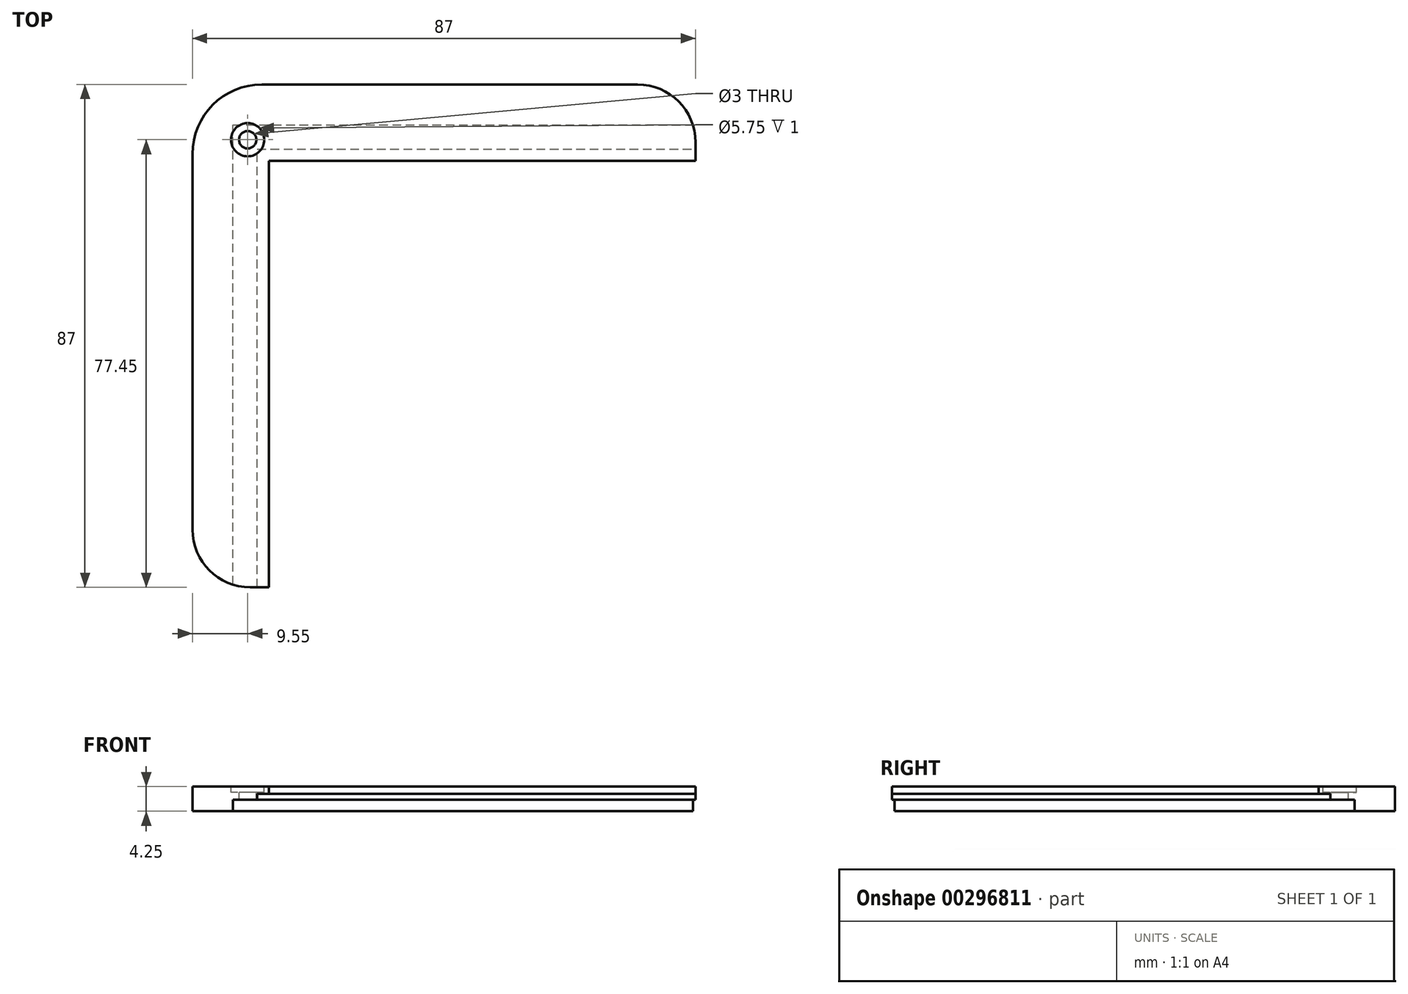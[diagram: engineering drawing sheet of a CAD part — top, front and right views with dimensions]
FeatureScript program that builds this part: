
annotation { "Feature Type Name" : "Feature", "Feature Type Description" : "" }
export const myFeature = defineFeature(function(context is Context, id is Id, definition is map)
    precondition{}
    {
        {
            var Q0;
            Q0=qCreatedBy(makeId("Front.planeOp"),FACE);
            var sketch = newSketch(context, id + "F0", { "sketchPlane" : qUnion([Q0])});
            skLineSegment(sketch, "E0", {"start": v(-6.2, -1) * mm, "end": v(-6.2, -3) * mm});
            skLineSegment(sketch, "E1", {"start": v(-6.2, -3) * mm, "end": v(-13.2, -3) * mm});
            skLineSegment(sketch, "E2", {"start": v(-13.2, -3) * mm, "end": v(-13.2, 1.25) * mm});
            skLineSegment(sketch, "E3", {"start": v(-13.2, 1.25) * mm, "end": v(0, 1.25) * mm});
            skLineSegment(sketch, "E4", {"start": v(0, 1.25) * mm, "end": v(0, 0) * mm});
            skLineSegment(sketch, "E5", {"start": v(-6.2, -1) * mm, "end": v(-2, -1) * mm});
            skLineSegment(sketch, "E6", {"start": v(-2, -1) * mm, "end": v(-2, 0) * mm});
            skLineSegment(sketch, "E7", {"start": v(-2, 0) * mm, "end": v(0, 0) * mm});
            skSolve(sketch);
        }
        {
            var Q0;
            Q0=qCreatedBy(makeId("Top.planeOp"),FACE);
            var sketch = newSketch(context, id + "F1", { "sketchPlane" : qUnion([Q0])});
            skPoint(sketch, "E8.0", {"position": v(-6.2, 0) * mm});
            skLineSegment(sketch, "E9", {"start": v(-6.2, 0) * mm, "end": v(-6.2, 80) * mm});
            skLineSegment(sketch, "E10", {"start": v(-6.2, 80) * mm, "end": v(73.8, 80) * mm});
            skSolve(sketch);
        }
        {
            var Q0;
            Q0 = qSketchRegion(id + "F0", true);
            var Q1;
            Q1 = qConstructionFilter(qBodyType(qCreatedBy(id + "F1" ,EDGE), BodyType.WIRE), ConstructionObject.NO);
            sweep(context, id + "F2", {"profiles" : qUnion([Q0]), "path" : qUnion([Q1])});
        }
        {
            var Q0;
            Q0=makeQuery(id+"F2.opSweep","CAP_EDGE",EDGE,{"disambiguationData":[OSD([sQuery(id+"F0.wireOp",EDGE,"E2"),sQuery(id+"F1.wireOp",VERTEX,"E9.start")])],"isStart":true});
            var Q1;
            Q1=makeQuery(id+"F2.opSweep","CAP_EDGE",EDGE,{"disambiguationData":[OSD([sQuery(id+"F0.wireOp",EDGE,"E2"),sQuery(id+"F1.wireOp",VERTEX,"E10.end")])],"isStart":false});
            fillet(context, id + "F3", {"entities" : qUnion([Q0, Q1]), "radius" : 10 * mm, "tangentPropagation" : true, "allowEdgeOverflow" : false});
        }
        {
            var Q0;
            Q0=makeQuery(id+"F2.opSweep","MID_CAP_EDGE",EDGE,{"disambiguationData":[OSD([sQuery(id+"F0.wireOp",EDGE,"E2"),sQuery(id+"F1.wireOp",VERTEX,"E10.start")])],"capPos":1.0});
            fillet(context, id + "F4", {"entities" : qUnion([Q0]), "radius" : 12 * mm, "tangentPropagation" : true, "allowEdgeOverflow" : false});
        }
        {
            var Q0;
            Q0=makeQuery(id+"F2.opSweep","SWEPT_FACE",FACE,{"disambiguationData":[OSD([sQuery(id+"F0.wireOp",EDGE,"E3"),sQuery(id+"F1.wireOp",EDGE,"E9")])]});
            var sketch = newSketch(context, id + "F5", { "sketchPlane" : qUnion([Q0])});
            skPoint(sketch, "E11.0", {"position": v(-6.2, 80) * mm});
            skLineSegment(sketch, "E12.bottom", {"start": v(-6.2, 80) * mm, "end": v(-3.65, 80) * mm, "construction": true});
            skLineSegment(sketch, "E12.top", {"start": v(-6.2, 77.45) * mm, "end": v(-3.65, 77.45) * mm, "construction": true});
            skLineSegment(sketch, "E12.left", {"start": v(-6.2, 80) * mm, "end": v(-6.2, 77.45) * mm, "construction": true});
            skLineSegment(sketch, "E12.right", {"start": v(-3.65, 80) * mm, "end": v(-3.65, 77.45) * mm, "construction": true});
            skPoint(sketch, "E13", {"position": v(-3.65, 77.45) * mm});
            skSolve(sketch);
        }
        {
            var Q0;
            Q0=sQuery(id+"F5.wireOp",VERTEX,"E13");
            var Q1;
            Q1=makeQuery(id+"F2.opSweep","SWEPT_BODY",BODY,{"disambiguationData":[OSD([sQuery(id+"F0.wireOp",EDGE,"E0"),sQuery(id+"F0.wireOp",EDGE,"E1"),sQuery(id+"F0.wireOp",EDGE,"E2"),sQuery(id+"F0.wireOp",EDGE,"E3"),sQuery(id+"F0.wireOp",EDGE,"E4"),sQuery(id+"F0.wireOp",EDGE,"E5"),sQuery(id+"F0.wireOp",EDGE,"E6"),sQuery(id+"F0.wireOp",EDGE,"E7"),sQuery(id+"F1.wireOp",EDGE,"E10")])]});
            hole(context, id + "F6", {"style" : HoleStyle.C_BORE, "endStyle" : HoleEndStyle.THROUGH, "holeDiameter" : 3 * mm, "cBoreDiameter" : 5.75 * mm, "cBoreDepth" : 1 * mm, "tappedDepth" : 12 * mm, "tapClearance" : 3, "startFromSketch" : true, "locations" : qUnion([Q0]), "scope" : qUnion([Q1])});
        }
    });
